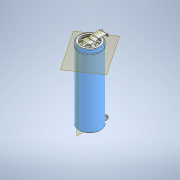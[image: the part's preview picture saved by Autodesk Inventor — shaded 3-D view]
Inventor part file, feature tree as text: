
AUTODESK INVENTOR PART (.ipt)
format: ipt  version: 2020 (Build 240168000, 168)  size: 635,392 bytes
history: native  units: mm
features: sketch x6, plane x4, extrude x3, fillet x3, revolve x1, other x1
ambient origin geometry x8: Origin, YZ Plane, XZ Plane, XY Plane, X Axis, Y Axis, Z Axis, Center Point
bodies: Solid1 (feature_tree), Solid2 (feature_tree), Body1 (feature_tree), Body2 (feature_tree)
feature tree (18):
  extrude  "Extrusion1"  Depth=10.0mm TaperAngle=0.0deg
  plane  "Work Plane3"
  extrude  "Extrusion2"  [1 undecoded]
  plane  "Work Plane4"
  revolve  "Revolution1"  [1 undecoded]
  fillet  "Fillet1"  [1 undecoded]
  extrude  "Extrusion3"  Depth=1.0mm
  fillet  "Fillet2"  Radius=1.0mm
  fillet  "Fillet4"  Radius=0.12mm
  sketch  "Sketch5"  dims[d16=0.12mm]
  plane  "Work Plane2"
  sketch  "Sketch2"  dims[d4=-3.0mm d5=-4.0mm]
  sketch  "Sketch1"  dims[d0=2.0mm d1=0.0mm d2=10.0mm d3=0.0mm]
  plane  "Work Plane1"
  sketch  "Sketch3"  dims[d6=19.4mm d7=1.0mm d8=0.0mm d9=90.0deg]
  other  "Work Axis1"
  sketch  "Sketch4"  dims[d10=0.1mm d11=0.12mm d13=1.0mm d14=0.12mm]
  sketch  "Sketch6"  dims[d17=3.0mm d18=3.6mm d19=7.0mm d20=0.0mm d21=2.0mm d26=3.2mm d27=1.6mm d28=9.0mm d29=1.0mm]
note: 3 required parameter values undecoded (feature->parameter linkage not recoverable at this tier; creation-order binding heuristic only, values carry confidence <= 0.55)